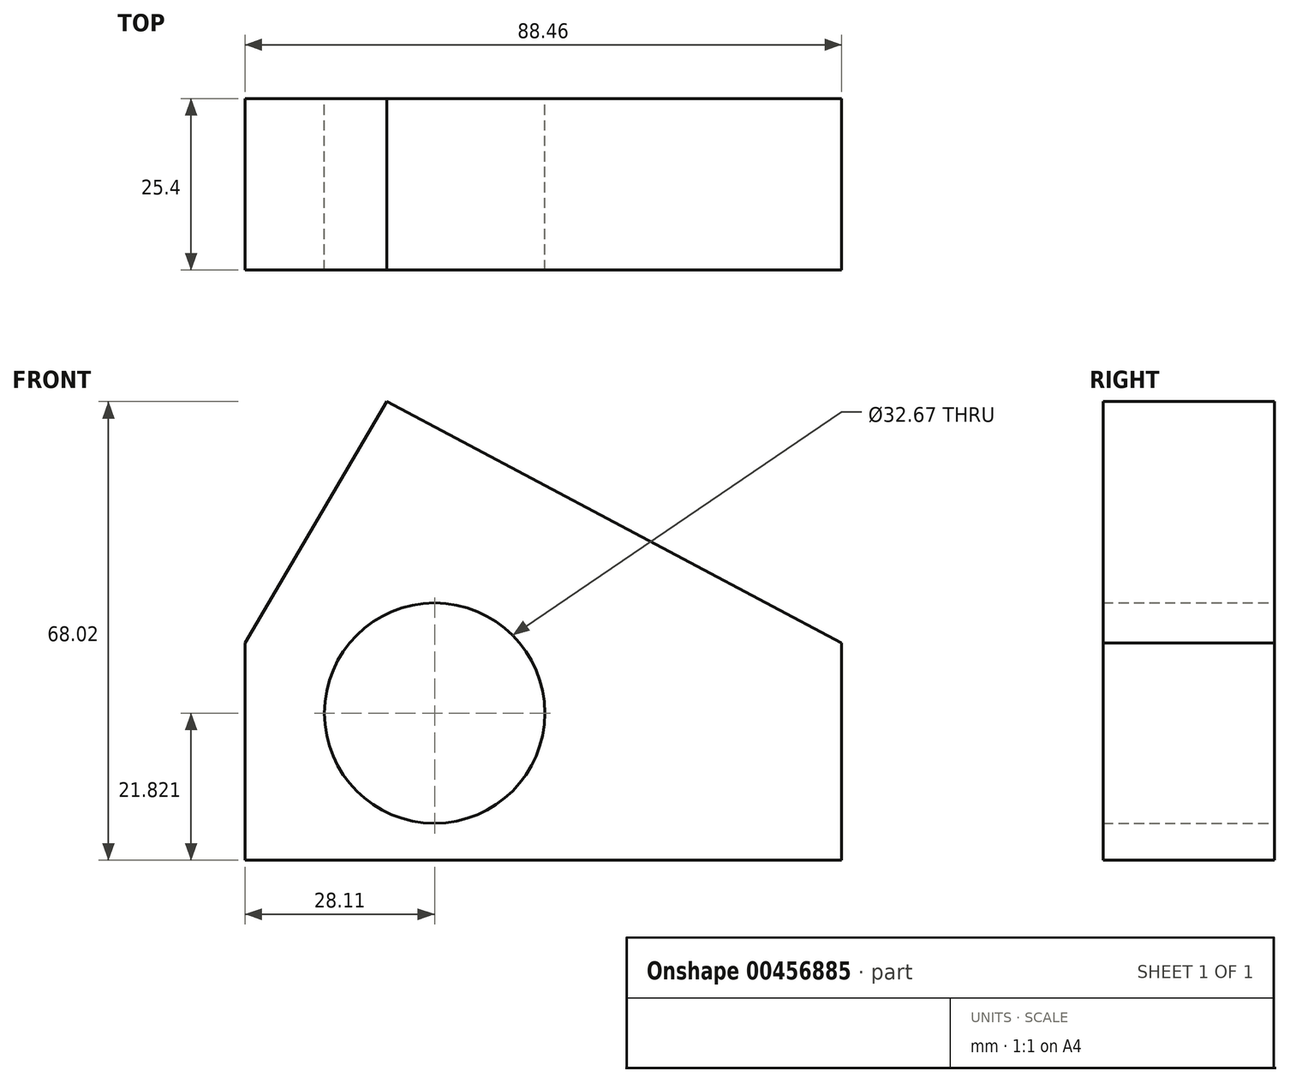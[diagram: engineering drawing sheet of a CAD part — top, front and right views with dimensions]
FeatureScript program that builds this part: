
annotation { "Feature Type Name" : "Feature", "Feature Type Description" : "" }
export const myFeature = defineFeature(function(context is Context, id is Id, definition is map)
    precondition{}
    {
        {
            var Q0;
            Q0=qCreatedBy(makeId("Front.planeOp"),FACE);
            var sketch = newSketch(context, id + "F0", { "sketchPlane" : qUnion([Q0])});
            skLineSegment(sketch, "E0.bottom", {"start": v(-44.23, 16.12) * mm, "end": v(44.23, 16.12) * mm});
            skLineSegment(sketch, "E0.top", {"start": v(-44.23, -16.12) * mm, "end": v(44.23, -16.12) * mm});
            skLineSegment(sketch, "E0.left", {"start": v(-44.23, 16.12) * mm, "end": v(-44.23, -16.12) * mm});
            skLineSegment(sketch, "E0.right", {"start": v(44.23, 16.12) * mm, "end": v(44.23, -16.12) * mm});
            skPoint(sketch, "E0.middle", {"position": v(0, 0) * mm});
            skLineSegment(sketch, "E1", {"start": v(-44.23, 16.12) * mm, "end": v(-23.2, 51.9) * mm});
            skLineSegment(sketch, "E2", {"start": v(-23.2, 51.9) * mm, "end": v(44.23, 16.12) * mm});
            skCircle(sketch, "E3", {"center": v(-16.12, 5.7) * mm, "radius": 16.34 * mm});
            skSolve(sketch);
        }
        {
            var Q0;
            Q0 = qSketchRegion(id + "F0", true);
            var Q1;
            Q1 = qSketchRegion(id + "F3uxuXpvfocCzP4_1", true);
            extrude(context, id + "F1", {"entities" : qUnion([Q0, Q1]), "depth" : 25.4 * mm});
        }
    });
